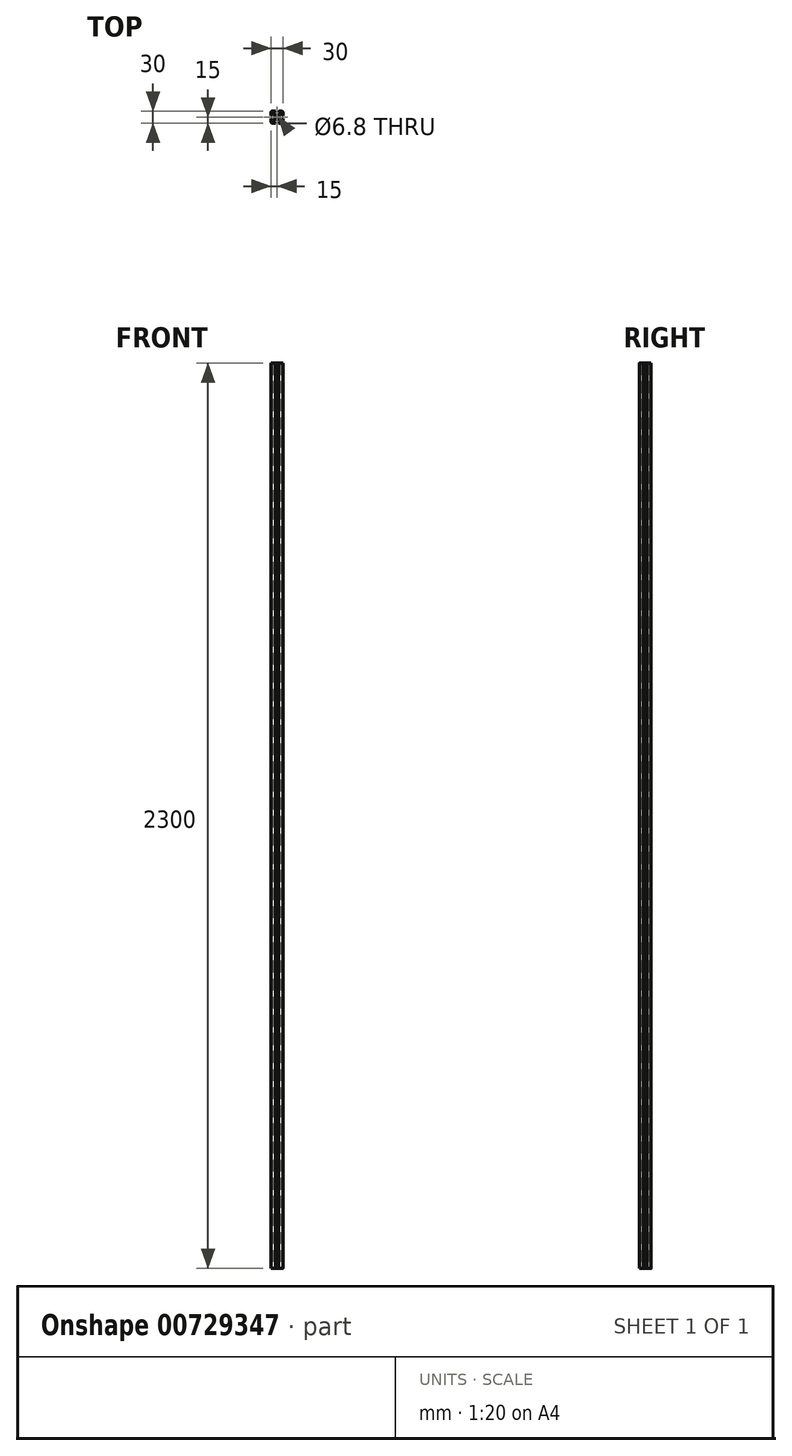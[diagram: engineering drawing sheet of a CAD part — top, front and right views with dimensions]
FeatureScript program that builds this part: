
annotation { "Feature Type Name" : "Feature", "Feature Type Description" : "" }
export const myFeature = defineFeature(function(context is Context, id is Id, definition is map)
    precondition{}
    {
        {
            var Q0;
            Q0=qCreatedBy(makeId("Top.planeOp"),FACE);
            var sketch = newSketch(context, id + "F0", { "sketchPlane" : qUnion([Q0])});
            skLineSegment(sketch, "E0.top", {"start": v(-15, 15) * mm, "end": v(-4.1, 15) * mm});
            skLineSegment(sketch, "E1", {"start": v(-4.1, 15) * mm, "end": v(-4.1, 12.8) * mm});
            skLineSegment(sketch, "E2", {"start": v(-4.1, 12.8) * mm, "end": v(-8.25, 12.8) * mm});
            skLineSegment(sketch, "E3", {"start": v(-8.25, 12.8) * mm, "end": v(-8.25, 9.66) * mm});
            skLineSegment(sketch, "E4", {"start": v(8.25, 9.66) * mm, "end": v(8.25, 12.8) * mm});
            skLineSegment(sketch, "E5", {"start": v(8.25, 12.8) * mm, "end": v(4.1, 12.8) * mm});
            skLineSegment(sketch, "E6", {"start": v(4.1, 12.8) * mm, "end": v(4.1, 15) * mm});
            skLineSegment(sketch, "E7", {"start": v(0, 15) * mm, "end": v(0, 5.6) * mm, "construction": true});
            skLineSegment(sketch, "E8.trimOffspring", {"start": v(4.1, 15) * mm, "end": v(15, 15) * mm});
            skLineSegment(sketch, "E9.trimOffspring", {"start": v(-15, 4.1) * mm, "end": v(-15, 15) * mm});
            skLineSegment(sketch, "E10.trimOffspring", {"start": v(15, 4.1) * mm, "end": v(15, 15) * mm});
            skLineSegment(sketch, "E11", {"start": v(-8.25, 9.66) * mm, "end": v(-4.19, 5.6) * mm});
            skLineSegment(sketch, "E12", {"start": v(-4.19, 5.6) * mm, "end": v(4.19, 5.6) * mm});
            skLineSegment(sketch, "E13", {"start": v(4.19, 5.6) * mm, "end": v(8.25, 9.66) * mm});
            skLineSegment(sketch, "E14", {"start": v(0, 0) * mm, "end": v(0, 0) * mm});
            skLineSegment(sketch, "E15", {"start": v(0, 0) * mm, "end": v(-15, 15) * mm, "construction": true});
            skLineSegment(sketch, "E16.1.0", {"start": v(-12.8, -4.1) * mm, "end": v(-12.8, -8.25) * mm});
            skLineSegment(sketch, "E16.1.1", {"start": v(-15, -4.1) * mm, "end": v(-12.8, -4.1) * mm});
            skLineSegment(sketch, "E16.1.2", {"start": v(-15, -15) * mm, "end": v(-15, -4.1) * mm});
            skLineSegment(sketch, "E16.1.3", {"start": v(-4.1, -15) * mm, "end": v(-15, -15) * mm});
            skLineSegment(sketch, "E16.1.4", {"start": v(-12.8, -8.25) * mm, "end": v(-9.66, -8.25) * mm});
            skLineSegment(sketch, "E16.1.5", {"start": v(-9.66, -8.25) * mm, "end": v(-5.6, -4.19) * mm});
            skLineSegment(sketch, "E16.1.6", {"start": v(-5.6, -4.19) * mm, "end": v(-5.6, 4.19) * mm});
            skLineSegment(sketch, "E16.1.7", {"start": v(-5.6, 4.19) * mm, "end": v(-9.66, 8.25) * mm});
            skLineSegment(sketch, "E16.1.8", {"start": v(-9.66, 8.25) * mm, "end": v(-12.8, 8.25) * mm});
            skLineSegment(sketch, "E16.1.9", {"start": v(-12.8, 8.25) * mm, "end": v(-12.8, 4.1) * mm});
            skLineSegment(sketch, "E16.1.10", {"start": v(-12.8, 4.1) * mm, "end": v(-15, 4.1) * mm});
            skLineSegment(sketch, "E16.2.0", {"start": v(4.1, -12.8) * mm, "end": v(8.25, -12.8) * mm});
            skLineSegment(sketch, "E16.2.1", {"start": v(4.1, -15) * mm, "end": v(4.1, -12.8) * mm});
            skLineSegment(sketch, "E16.2.2", {"start": v(15, -15) * mm, "end": v(4.1, -15) * mm});
            skLineSegment(sketch, "E16.2.3", {"start": v(15, -4.1) * mm, "end": v(15, -15) * mm});
            skLineSegment(sketch, "E16.2.4", {"start": v(8.25, -12.8) * mm, "end": v(8.25, -9.66) * mm});
            skLineSegment(sketch, "E16.2.5", {"start": v(8.25, -9.66) * mm, "end": v(4.19, -5.6) * mm});
            skLineSegment(sketch, "E16.2.6", {"start": v(4.19, -5.6) * mm, "end": v(-4.19, -5.6) * mm});
            skLineSegment(sketch, "E16.2.7", {"start": v(-4.19, -5.6) * mm, "end": v(-8.25, -9.66) * mm});
            skLineSegment(sketch, "E16.2.8", {"start": v(-8.25, -9.66) * mm, "end": v(-8.25, -12.8) * mm});
            skLineSegment(sketch, "E16.2.9", {"start": v(-8.25, -12.8) * mm, "end": v(-4.1, -12.8) * mm});
            skLineSegment(sketch, "E16.2.10", {"start": v(-4.1, -12.8) * mm, "end": v(-4.1, -15) * mm});
            skPoint(sketch, "E16.center", {"position": v(0, 0) * mm});
            skLineSegment(sketch, "E16.anchor1", {"start": v(-8.25, 12.8) * mm, "end": v(0, 0) * mm, "construction": true});
            skLineSegment(sketch, "E16.anchor2", {"start": v(12.8, 8.25) * mm, "end": v(0, 0) * mm, "construction": true});
            skLineSegment(sketch, "E17.2.3.0", {"start": v(12.8, 4.1) * mm, "end": v(12.8, 8.25) * mm});
            skLineSegment(sketch, "E17.3.3.0", {"start": v(15, 4.1) * mm, "end": v(12.8, 4.1) * mm});
            skLineSegment(sketch, "E17.6.3.0", {"start": v(15, 15) * mm, "end": v(15, 4.1) * mm});
            skLineSegment(sketch, "E17.12.3.0", {"start": v(12.8, 8.25) * mm, "end": v(9.66, 8.25) * mm});
            skLineSegment(sketch, "E17.15.3.0", {"start": v(9.66, 8.25) * mm, "end": v(5.6, 4.19) * mm});
            skLineSegment(sketch, "E17.18.3.0", {"start": v(5.6, 4.19) * mm, "end": v(5.6, -4.19) * mm});
            skLineSegment(sketch, "E17.21.3.0", {"start": v(5.6, -4.19) * mm, "end": v(9.66, -8.25) * mm});
            skLineSegment(sketch, "E17.24.3.0", {"start": v(9.66, -8.25) * mm, "end": v(12.8, -8.25) * mm});
            skLineSegment(sketch, "E17.27.3.0", {"start": v(12.8, -8.25) * mm, "end": v(12.8, -4.1) * mm});
            skLineSegment(sketch, "E17.30.3.0", {"start": v(12.8, -4.1) * mm, "end": v(15, -4.1) * mm});
            skCircle(sketch, "E18", {"center": v(0, 0) * mm, "radius": 3.4 * mm});
            skSolve(sketch);
        }
        {
            var Q0;
            Q0 = qSketchRegion(id + "F0", true);
            extrude(context, id + "F1", {"entities" : qUnion([Q0]), "depth" : 2300 * mm, "offsetDistance" : 25 * mm});
        }
        {
            var Q0;
            Q0=makeQuery(id+"F1.opExtrude","SWEPT_EDGE",EDGE,{"disambiguationData":[OSD([sQuery(id+"F0.wireOp",EDGE,"E16.2.2"),sQuery(id+"F0.wireOp",EDGE,"E16.2.3")])]});
            var Q1;
            Q1=makeQuery(id+"F1.opExtrude","SWEPT_EDGE",EDGE,{"disambiguationData":[OSD([sQuery(id+"F0.wireOp",EDGE,"E17.6.3.0"),sQuery(id+"F0.wireOp",EDGE,"E8.trimOffspring")])]});
            var Q2;
            Q2=makeQuery(id+"F1.opExtrude","SWEPT_EDGE",EDGE,{"disambiguationData":[OSD([sQuery(id+"F0.wireOp",EDGE,"E16.1.2"),sQuery(id+"F0.wireOp",EDGE,"E16.1.3")])]});
            var Q3;
            Q3=makeQuery(id+"F1.opExtrude","SWEPT_EDGE",EDGE,{"disambiguationData":[OSD([sQuery(id+"F0.wireOp",EDGE,"E0.top"),sQuery(id+"F0.wireOp",EDGE,"E9.trimOffspring")])]});
            fillet(context, id + "F2", {"entities" : qUnion([Q0, Q1, Q2, Q3]), "radius" : 3 * mm, "tangentPropagation" : true, "allowEdgeOverflow" : false});
        }
    });
